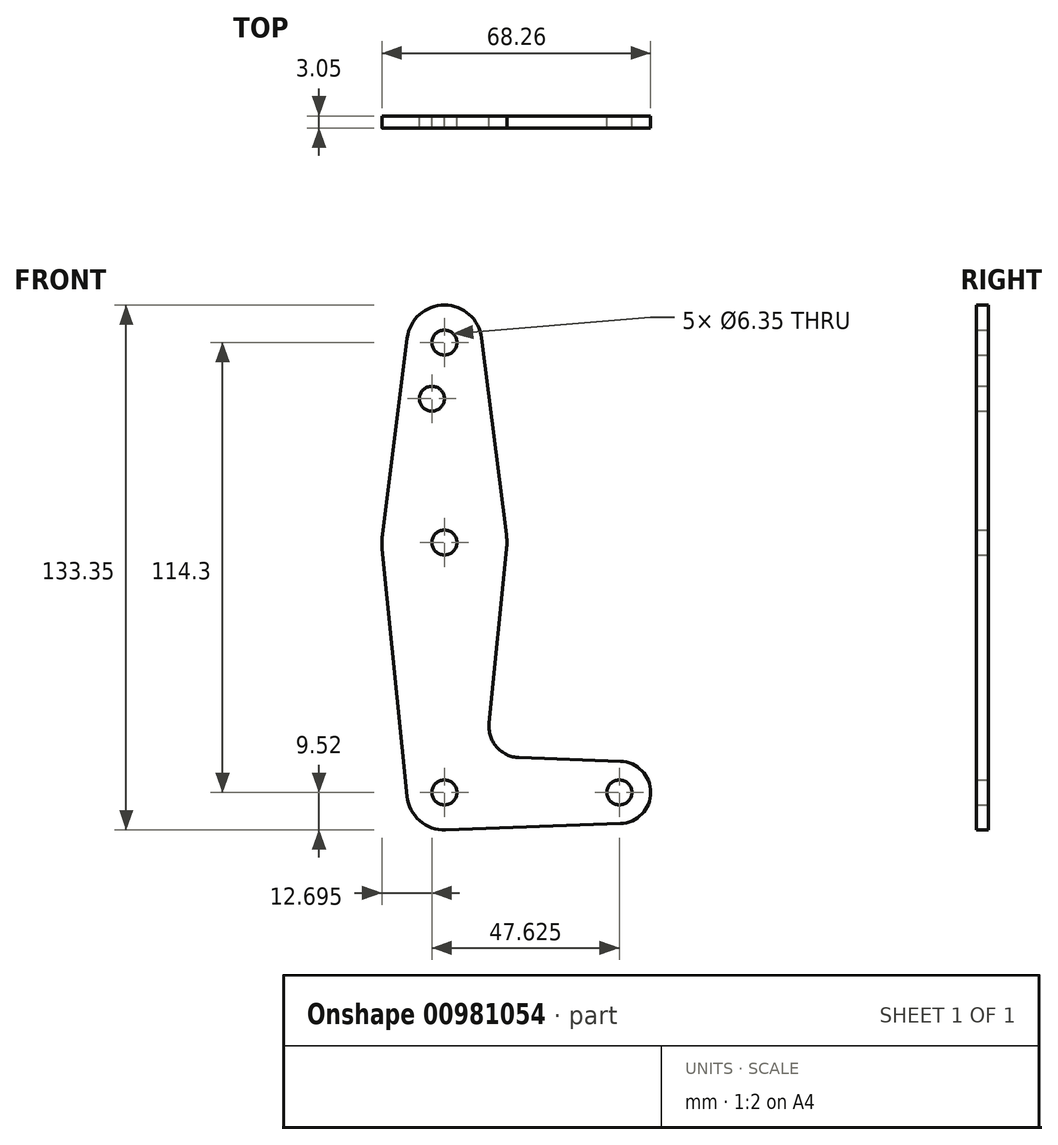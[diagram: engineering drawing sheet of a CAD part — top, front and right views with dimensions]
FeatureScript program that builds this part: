
annotation { "Feature Type Name" : "Feature", "Feature Type Description" : "" }
export const myFeature = defineFeature(function(context is Context, id is Id, definition is map)
    precondition{}
    {
        {
            var Q0;
            Q0=qCreatedBy(makeId("Front.planeOp"),FACE);
            var sketch = newSketch(context, id + "F0", { "sketchPlane" : qUnion([Q0])});
            skLineSegment(sketch, "E0", {"start": v(0, 0) * mm, "end": v(44.45, 0) * mm});
            skLineSegment(sketch, "E1", {"start": v(44.45, 0) * mm, "end": v(0, 0) * mm, "construction": true});
            skLineSegment(sketch, "E2", {"start": v(0, 0) * mm, "end": v(0, 114.3) * mm, "construction": true});
            skCircle(sketch, "E3", {"center": v(0, 114.3) * mm, "radius": 9.53 * mm});
            skCircle(sketch, "E4", {"center": v(44.45, 0) * mm, "radius": 7.94 * mm});
            skCircle(sketch, "E5", {"center": v(0, 63.5) * mm, "radius": 15.88 * mm});
            skCircle(sketch, "E6", {"center": v(0, 0) * mm, "radius": 9.53 * mm});
            skLineSegment(sketch, "E7", {"start": v(9.45, 115.5) * mm, "end": v(15.75, 65.48) * mm});
            skLineSegment(sketch, "E8", {"start": v(-9.45, 115.5) * mm, "end": v(-15.75, 65.48) * mm});
            skLineSegment(sketch, "E9", {"start": v(-15.8, 61.91) * mm, "end": v(-9.48, -0.95) * mm});
            skLineSegment(sketch, "E10", {"start": v(15.8, 61.91) * mm, "end": v(11.34, 17.6) * mm});
            skLineSegment(sketch, "E11", {"start": v(44.73, 7.93) * mm, "end": v(18.97, 8.85) * mm});
            skLineSegment(sketch, "E12", {"start": v(0.34, -9.52) * mm, "end": v(44.73, -7.93) * mm});
            skCircle(sketch, "E13", {"center": v(0, 114.3) * mm, "radius": 3.18 * mm});
            skCircle(sketch, "E14", {"center": v(0, 63.5) * mm, "radius": 3.18 * mm});
            skCircle(sketch, "E15", {"center": v(0, 0) * mm, "radius": 3.18 * mm});
            skCircle(sketch, "E16", {"center": v(44.45, 0) * mm, "radius": 3.18 * mm});
            skCircle(sketch, "E17", {"center": v(-3.17, 100.03) * mm, "radius": 3.18 * mm});
            skArc(sketch, "E18.filletArc", {"start": v(11.34, 17.6) * mm, "mid": v(13.26, 11.57) * mm, "end": v(18.97, 8.85) * mm});
            skSolve(sketch);
        }
        {
            var Q0;
            {var subQ1=sQuery(id+"F0.wireOp",EDGE,"E7");Q0=makeQuery(id+"F0.imprint","IMPRINT",FACE,{"disambiguationData":[TD([[makeQuery(id+"F0.imprint","IMPRINT",EDGE,{"derivedFrom":subQ1}),-1.0]])]});}
            var Q1;
            Q1=makeQuery(id+"F0.imprint","IMPRINT",FACE,{"disambiguationData":[TD([[makeQuery(id+"F0.imprint","IMPRINT",EDGE,{"derivedFrom":sQuery(id+"F0.wireOp",EDGE,"E13")}),-1.0]])]});
            var Q2;
            Q2=makeQuery(id+"F0.imprint","IMPRINT",FACE,{"disambiguationData":[TD([[makeQuery(id+"F0.imprint","IMPRINT",EDGE,{"derivedFrom":sQuery(id+"F0.wireOp",EDGE,"E14")}),-1.0]])]});
            var Q3;
            {var subQ0=sQuery(id+"F0.wireOp",EDGE,"E9");Q3=makeQuery(id+"F0.imprint","IMPRINT",FACE,{"disambiguationData":[TD([[makeQuery(id+"F0.imprint","IMPRINT",EDGE,{"derivedFrom":subQ0}),1.0]])]});}
            var Q4;
            {var subQ5=sQuery(id+"F0.wireOp",EDGE,"E12");Q4=makeQuery(id+"F0.imprint","IMPRINT",FACE,{"disambiguationData":[TD([[makeQuery(id+"F0.imprint","IMPRINT",EDGE,{"derivedFrom":subQ5}),1.0]])]});}
            var Q5;
            Q5=makeQuery(id+"F0.imprint","IMPRINT",FACE,{"disambiguationData":[TD([[makeQuery(id+"F0.imprint","IMPRINT",EDGE,{"derivedFrom":sQuery(id+"F0.wireOp",EDGE,"E16")}),-1.0]])]});
            var Q6;
            Q6=makeQuery(id+"F0.imprint","IMPRINT",FACE,{"disambiguationData":[TD([[makeQuery(id+"F0.imprint","IMPRINT",EDGE,{"derivedFrom":sQuery(id+"F0.wireOp",EDGE,"E15")}),-1.0]])]});
            extrude(context, id + "F1", {"entities" : qUnion([Q0, Q1, Q2, Q3, Q4, Q5, Q6]), "depth" : 3.05 * mm, "offsetDistance" : 25.4 * mm});
        }
    });
